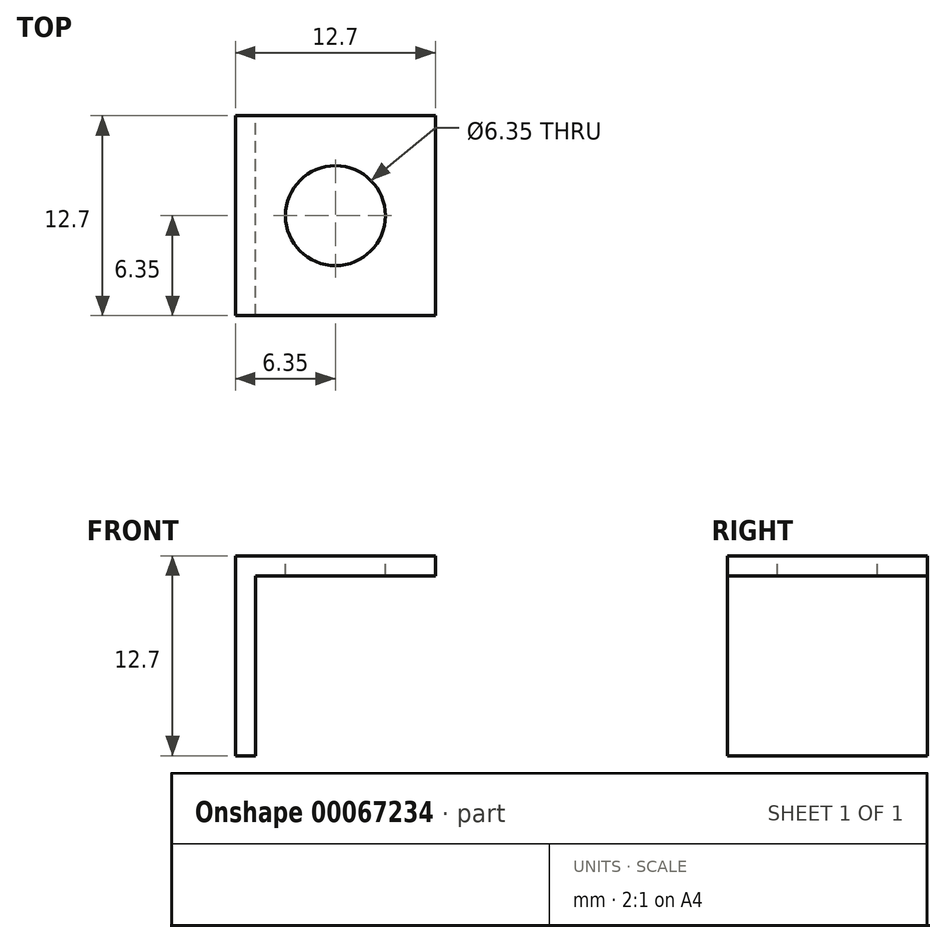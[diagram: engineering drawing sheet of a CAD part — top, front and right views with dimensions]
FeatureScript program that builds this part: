
annotation { "Feature Type Name" : "Feature", "Feature Type Description" : "" }
export const myFeature = defineFeature(function(context is Context, id is Id, definition is map)
    precondition{}
    {
        {
            var Q0;
            Q0=qCreatedBy(makeId("Front.planeOp"),FACE);
            var sketch = newSketch(context, id + "F0", { "sketchPlane" : qUnion([Q0])});
            skLineSegment(sketch, "E0", {"start": v(0, 0) * mm, "end": v(0, 12.7) * mm});
            skLineSegment(sketch, "E1", {"start": v(0, 12.7) * mm, "end": v(12.7, 12.7) * mm});
            skLineSegment(sketch, "E2", {"start": v(12.7, 12.7) * mm, "end": v(12.7, 11.43) * mm});
            skLineSegment(sketch, "E3", {"start": v(12.7, 11.43) * mm, "end": v(1.27, 11.43) * mm});
            skLineSegment(sketch, "E4", {"start": v(1.27, 11.43) * mm, "end": v(1.27, 0) * mm});
            skLineSegment(sketch, "E5", {"start": v(1.27, 0) * mm, "end": v(0, 0) * mm});
            skSolve(sketch);
        }
        {
            var Q0;
            Q0=makeQuery(id+"F0.imprint","IMPRINT",FACE,{"disambiguationData":[TD([[makeQuery(id+"F0.imprint","IMPRINT",EDGE,{"derivedFrom":sQuery(id+"F0.wireOp",EDGE,"E0")}),-1.0]])]});
            extrude(context, id + "F1", {"entities" : qUnion([Q0]), "depth" : 12.7 * mm, "symmetric" : true});
        }
        {
            var Q0;
            Q0=makeQuery(id+"F1.opExtrude","SWEPT_FACE",FACE,{"disambiguationData":[OSD([sQuery(id+"F0.wireOp",EDGE,"E1")])]});
            var sketch = newSketch(context, id + "F2", { "sketchPlane" : qUnion([Q0])});
            skCircle(sketch, "E6", {"center": v(6.35, 0) * mm, "radius": 3.18 * mm});
            skSolve(sketch);
        }
        {
            var Q0;
            Q0=makeQuery(id+"F2.imprint","IMPRINT",FACE,{"disambiguationData":[TD([[makeQuery(id+"F2.imprint","IMPRINT",EDGE,{"derivedFrom":sQuery(id+"F2.wireOp",EDGE,"E6")}),1.0]])]});
            extrude(context, id + "F3", {"entities" : qUnion([Q0]), "operationType" : NewBodyOperationType.REMOVE, "oppositeDirection" : true, "depth" : 25.4 * mm});
        }
    });
